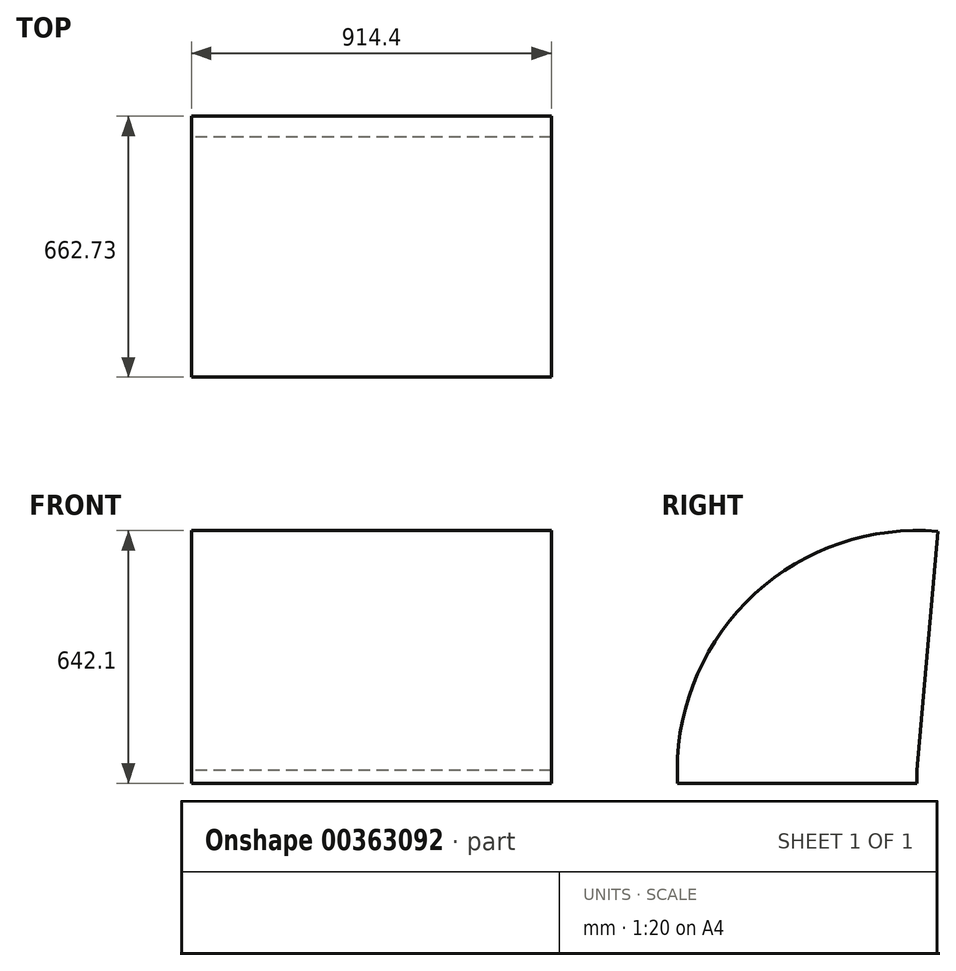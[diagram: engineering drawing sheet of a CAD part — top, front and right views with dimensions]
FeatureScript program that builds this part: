
annotation { "Feature Type Name" : "Feature", "Feature Type Description" : "" }
export const myFeature = defineFeature(function(context is Context, id is Id, definition is map)
    precondition{}
    {
        {
            assignVariable(context, id + "F0", {"name" : "hgt", "anyValue" : 32.5});
        }
        {
            assignVariable(context, id + "F1", {"name" : "max_lid_angle", "anyValue" : 95});
        }
        {
            var Q0;
            Q0=qCreatedBy(makeId("Top.planeOp"),FACE);
            var sketch = newSketch(context, id + "F2", { "sketchPlane" : qUnion([Q0])});
            skLineSegment(sketch, "E0.bottom", {"start": v(457.2, 304.8) * mm, "end": v(-457.2, 304.8) * mm});
            skLineSegment(sketch, "E0.top", {"start": v(457.2, -304.8) * mm, "end": v(-457.2, -304.8) * mm});
            skLineSegment(sketch, "E0.left", {"start": v(457.2, 304.8) * mm, "end": v(457.2, -304.8) * mm});
            skLineSegment(sketch, "E0.right", {"start": v(-457.2, 304.8) * mm, "end": v(-457.2, -304.8) * mm});
            skPoint(sketch, "E0.middle", {"position": v(0, 0) * mm});
            skPoint(sketch, "E1.visualSharp", {"position": v(-457.2, 304.8) * mm});
            skPoint(sketch, "E2.visualSharp", {"position": v(457.2, 304.8) * mm});
            skPoint(sketch, "E3.visualSharp", {"position": v(457.2, -304.8) * mm});
            skPoint(sketch, "E4.visualSharp", {"position": v(-457.2, -304.8) * mm});
            skSolve(sketch);
        }
        {
            var Q0;
            Q0 = qSketchRegion(id + "F2", true);
            extrude(context, id + "F3", {"entities" : qUnion([Q0]), "depth" : (getVariable(context, 'hgt')) * mm});
        }
        {
            var Q0;
            Q0=makeQuery(id+"F3.opExtrude","CAP_FACE",FACE,{"disambiguationData":[OSD([sQuery(id+"F2.wireOp",EDGE,"E0.bottom"),sQuery(id+"F2.wireOp",EDGE,"E0.top"),sQuery(id+"F2.wireOp",EDGE,"E0.left"),sQuery(id+"F2.wireOp",EDGE,"E0.right")])],"isStart":false});
            var sketch = newSketch(context, id + "F4", { "sketchPlane" : qUnion([Q0])});
            skLineSegment(sketch, "E5.bottom", {"start": v(-457.2, -304.8) * mm, "end": v(457.2, -304.8) * mm});
            skLineSegment(sketch, "E5.top", {"start": v(-457.2, 304.8) * mm, "end": v(457.2, 304.8) * mm});
            skLineSegment(sketch, "E5.left", {"start": v(-457.2, -304.8) * mm, "end": v(-457.2, 304.8) * mm});
            skLineSegment(sketch, "E5.right", {"start": v(457.2, -304.8) * mm, "end": v(457.2, 304.8) * mm});
            skSolve(sketch);
        }
        {
            var Q0;
            Q0 = qSketchRegion(id + "F4", true);
            var Q1;
            Q1=sQuery(id+"F4.wireOp",EDGE,"E5.top");
            revolve(context, id + "F5", {"operationType" : NewBodyOperationType.ADD, "entities" : qUnion([Q0]), "axis" : qUnion([Q1]), "revolveType" : RevolveType.ONE_DIRECTION, "oppositeDirection" : true, "angle" : (getVariable(context, 'max_lid_angle')) * degree});
        }
    });
